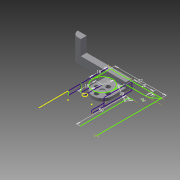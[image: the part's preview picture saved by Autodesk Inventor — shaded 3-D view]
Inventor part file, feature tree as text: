
AUTODESK INVENTOR PART (.ipt)
format: ipt  version: 2015 (Build 190159000, 159)  size: 244,736 bytes
history: native  units: in
note: dims shown in document units (in); Inventor stores cm internally (conversion verified against a paired STEP export)
features: sketch x22, extrude x15, pattern_linear x2, fillet x2, pattern_circular x1
ambient origin geometry x8: Origin, YZ Plane, XZ Plane, XY Plane, X Axis, Y Axis, Z Axis, Center Point
bodies: Solid1 (feature_tree)
feature tree (42):
  sketch  "Sketch1"  dims[d0=0.9449in d1=0.1969in]
  extrude  "Extrusion1"  Depth=0.1969in
  extrude  "Extrusion2"  Depth=0.9449in
  pattern_linear  "Rectangular Pattern1"  Count1=3  [1 undecoded]
  sketch  "Sketch4"  dims[d5=0.4921in d6=0.1969in]
  extrude  "Extrusion3"  Depth=0.1969in
  sketch  "Sketch6"  dims[d12=0.7874in d14=0.2362in d15=0.7874in d17=0.2362in]
  extrude  "Extrusion4"  Depth=0.315in TaperAngle=0.0deg
  extrude  "Extrusion5"  Depth=0.2362in
  extrude  "Extrusion6"  Depth=1.1756in
  pattern_circular  "Circular Pattern1"  Count=5  [1 undecoded]
  extrude  "Extrusion7"  Depth=0.7874in
  extrude  "Extrusion8"  Depth=0.7874in
  extrude  "Extrusion9"  Depth=0.1673in
  pattern_linear  "Rectangular Pattern2"  Count1=4 Spacing1=360.0deg
  sketch  "Sketch13"  dims[d35=0.1673in]
  fillet  "Fillet1"  Radius=0.0787in
  sketch  "Sketch14"  dims[d36=0.0394in d37=0.0in d38=1.5748in d39=360.0deg d42=0.0787in]
  sketch  "Sketch15"  dims[d45=0.7874in d47=0.7874in]
  sketch  "Sketch16"  dims[d52=0.1969in d63=0.1969in]
  extrude  "Extrusion10"  Depth=0.7874in
  extrude  "Extrusion11"  Depth=0.1969in
  extrude  "Extrusion12"  Depth=0.7087in
  extrude  "Extrusion13"  Depth=2.0472in
  extrude  "Extrusion14"  Depth=0.1969in
  sketch  "Sketch22"  dims[d77=0.1575in]
  fillet  "Fillet2"  Radius=0.7087in
  extrude  "Extrusion15"  Depth=0.7874in
  sketch  "Sketch2"  dims[d2=0.1673in d3=0.9449in d4=1.1811in]
  sketch  "Sketch5"  dims[d8=0.315in d9=0.0in d10=0.315in d11=0.0in]
  sketch  "Sketch7"  dims[d18=0.1969in d19=0.0in d20=1.1756in d23=1.9685in]
  sketch  "Sketch8"  dims[d25=0.7087in d26=0.7874in]
  sketch  "Sketch9"  dims[d27=0.7087in d28=0.7874in]
  sketch  "Sketch10"  dims[d29=0.1181in d30=0.0in d31=0.1673in]
  sketch  "Sketch11"  dims[d32=0.0394in d33=0.0in]
  sketch  "Sketch12"  dims[d34=0.2362in]
  sketch  "Sketch17"  dims[d66=2.0472in d67=0.7087in]
  sketch  "Sketch18"  dims[d68=0.7087in d69=2.0472in]
  sketch  "Sketch19"  dims[d70=0.7874in d71=0.1969in d72=0.7087in]
  sketch  "Sketch20"  dims[d73=2.0472in d74=0.7874in]
  sketch  "Sketch21"  dims[d75=0.315in d76=0.0in]
  sketch  "Sketch24"  dims[d78=0.9449in d79=0.0in d80=0.1673in d81=0.1673in d82=0.0in d83=1.1811in d85=0.2362in d86=0.1969in d87=0.0in d88=0.0in d89=0.0787in d90=0.1969in d91=0.0in d92=0.0787in d93=0.7874in d94=0.0in d95=0.7874in d96=0.0in d97=1.378in d98=0.0in d99=0.2362in d101=0.1181in d102=0.5906in d103=0.0in]
note: 2 required parameter values undecoded (feature->parameter linkage not recoverable at this tier; creation-order binding heuristic only, values carry confidence <= 0.55)
